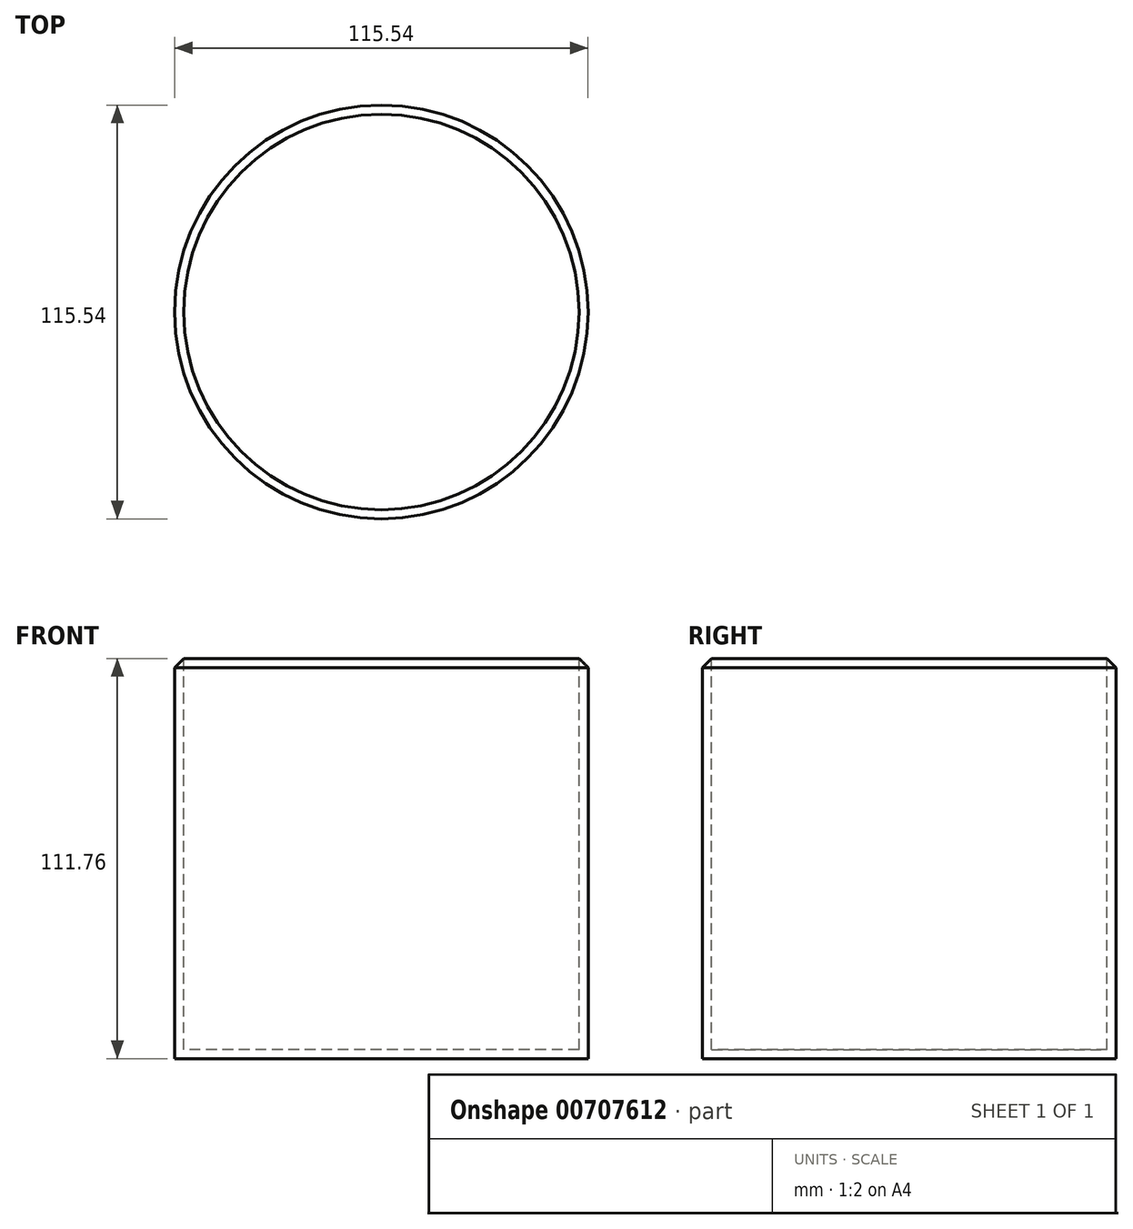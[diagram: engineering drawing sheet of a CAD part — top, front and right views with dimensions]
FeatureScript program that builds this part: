
annotation { "Feature Type Name" : "Feature", "Feature Type Description" : "" }
export const myFeature = defineFeature(function(context is Context, id is Id, definition is map)
    precondition{}
    {
        {
            var Q0;
            Q0=qCreatedBy(makeId("Top.planeOp"),FACE);
            var sketch = newSketch(context, id + "F0", { "sketchPlane" : qUnion([Q0])});
            skCircle(sketch, "E0", {"center": v(0, 0) * mm, "radius": 57.77 * mm});
            skSolve(sketch);
        }
        {
            var Q0;
            Q0 = qSketchRegion(id + "F0", true);
            extrude(context, id + "F1", {"entities" : qUnion([Q0]), "oppositeDirection" : true, "depth" : 114.3 * mm, "offsetDistance" : 25.4 * mm});
        }
        {
            var Q0;
            Q0=makeQuery(id+"F1.opExtrude","CAP_FACE",FACE,{"disambiguationData":[OSD([sQuery(id+"F0.wireOp",EDGE,"E0")])],"isStart":true});
            shell(context, id + "F2", {"entities" : qUnion([Q0]), "thickness" : 2.54 * mm});
        }
        {
            var Q0;
            Q0=makeQuery(id+"F1.opExtrude","CAP_EDGE",EDGE,{"disambiguationData":[OSD([sQuery(id+"F0.wireOp",EDGE,"E0")])],"isStart":true});
            chamfer(context, id + "F3", {"entities" : qUnion([Q0]), "width" : 5.08 * mm, "tangentPropagation" : true});
        }
        {
            var Q0;
            Q0=qCreatedBy(makeId("Right.planeOp"),FACE);
            var sketch = newSketch(context, id + "F4", { "sketchPlane" : qUnion([Q0])});
            skArc(sketch, "E1", {"start": v(58.58, -102.3) * mm, "mid": v(109.21, -61.92) * mm, "end": v(59.41, -20.52) * mm});
            skArc(sketch, "E2", {"start": v(59.2, -90.62) * mm, "mid": v(100.22, -60.6) * mm, "end": v(59.41, -30.3) * mm});
            skSolve(sketch);
        }
        {
            var Q0;
            Q0=sQuery(id+"F4.wireOp",EDGE,"E1");
            var Q1;
            Q1=sQuery(id+"F4.wireOp",EDGE,"E2");
            extrude(context, id + "F5", {"bodyType" : ToolBodyType.SURFACE, "surfaceEntities" : qUnion([Q0, Q1]), "depth" : 25.4 * mm, "offsetDistance" : 25.4 * mm});
        }
    });
